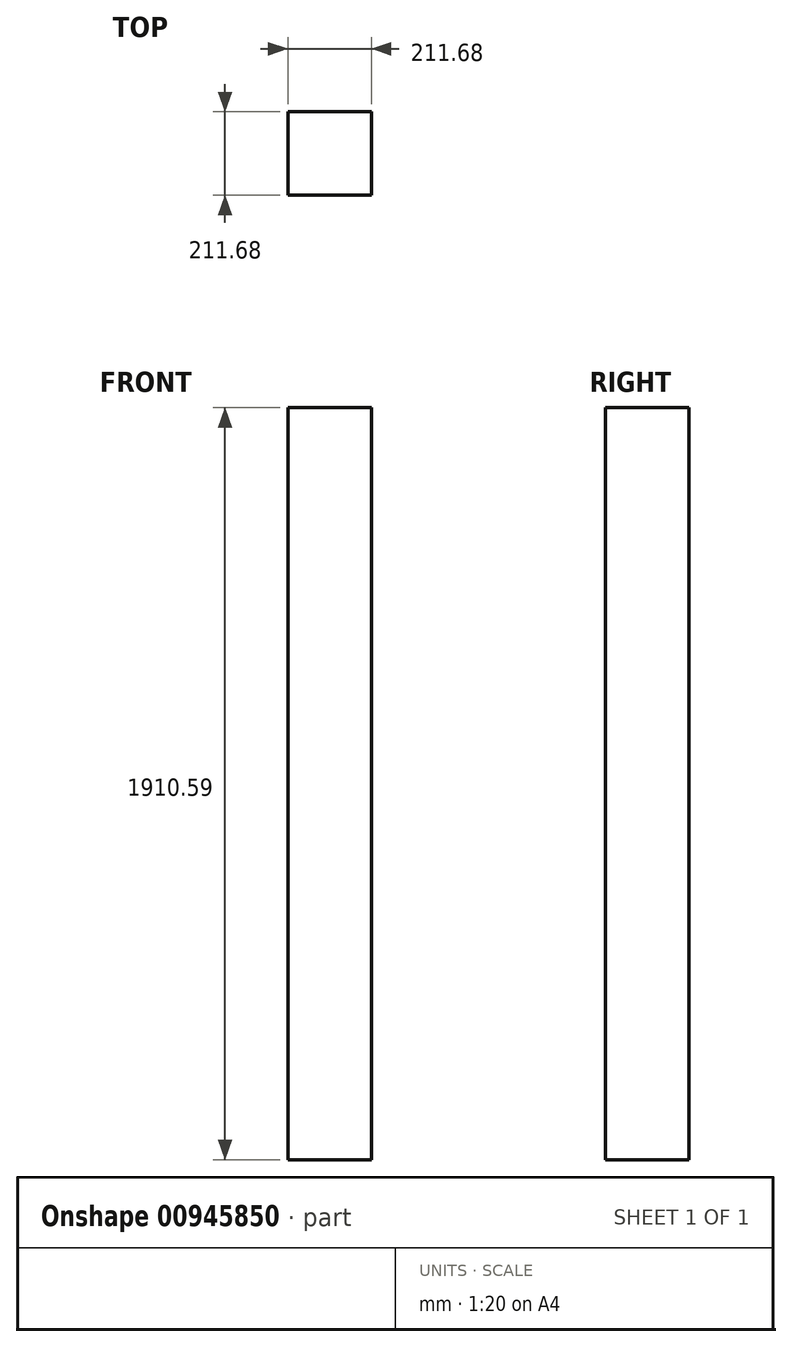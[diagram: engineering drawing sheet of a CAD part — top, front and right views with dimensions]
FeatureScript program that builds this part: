
annotation { "Feature Type Name" : "Feature", "Feature Type Description" : "" }
export const myFeature = defineFeature(function(context is Context, id is Id, definition is map)
    precondition{}
    {
        {
            var Q0;
            Q0=qCreatedBy(makeId("Top.planeOp"),FACE);
            var sketch = newSketch(context, id + "F0", { "sketchPlane" : qUnion([Q0])});
            skLineSegment(sketch, "E0.bottom", {"start": v(-211.68, 211.68) * mm, "end": v(0, 211.68) * mm});
            skLineSegment(sketch, "E0.top", {"start": v(-211.68, 0) * mm, "end": v(0, 0) * mm});
            skLineSegment(sketch, "E0.left", {"start": v(-211.68, 211.68) * mm, "end": v(-211.68, 0) * mm});
            skLineSegment(sketch, "E0.right", {"start": v(0, 211.68) * mm, "end": v(0, 0) * mm});
            skSolve(sketch);
        }
        {
            var Q0;
            Q0=makeQuery(id+"F0.imprint","IMPRINT",FACE,{"disambiguationData":[TD([[makeQuery(id+"F0.imprint","IMPRINT",EDGE,{"derivedFrom":sQuery(id+"F0.wireOp",EDGE,"E0.bottom")}),-1.0]])]});
            extrude(context, id + "F1", {"entities" : qUnion([Q0]), "depth" : 1910.6 * mm, "offsetDistance" : 25.4 * mm});
        }
    });
